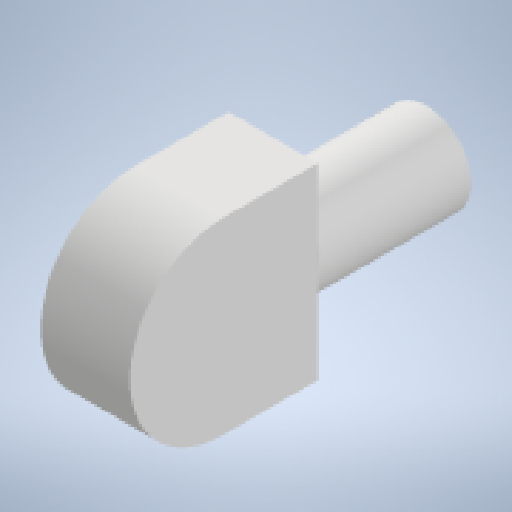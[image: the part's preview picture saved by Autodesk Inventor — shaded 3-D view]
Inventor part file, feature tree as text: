
AUTODESK INVENTOR PART (.ipt)
format: ipt  version: 2024 (Build 280153000, 153)  size: 216,064 bytes
history: native  units: in
note: dims shown in document units (in); Inventor stores cm internally (conversion verified against a paired STEP export)
features: extrude x3, fillet x3, sketch x3, other x1
ambient origin geometry x8: Origin, YZ Plane, XZ Plane, XY Plane, X Axis, Y Axis, Z Axis, Center Point
bodies: Solid1 (feature_tree)
feature tree (10):
  extrude  "Extrusion1"  Depth=1.9685in TaperAngle=0.0deg
  extrude  "Extrusion2"  Depth=2.4094in TaperAngle=0.0deg
  other  "Full Round Fillet1"
  fillet  "Face Fillet1"
  fillet  "Face Fillet2"
  fillet  "Fillet8"  Radius=1.2008in
  extrude  "Extrusion3"  Depth=0.0787in
  sketch  "Sketch1"  dims[d0=1.1417in d1=1.9685in d2=0.0in]
  sketch  "Sketch2"  dims[d3=2.4094in d4=2.4094in d5=0.0in d6=1.2008in]
  sketch  "Sketch3"  dims[d7=1.2008in d15=0.0787in d16=1.2992in d17=2.4094in d18=0.0in d8=0.0in d9=0.0in]
